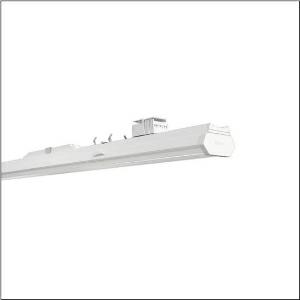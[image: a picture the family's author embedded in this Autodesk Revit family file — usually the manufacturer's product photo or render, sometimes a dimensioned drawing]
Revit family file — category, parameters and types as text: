
# Revit family: licross_21_protected_ho_52tp11mn4fxs
name_source: partatom
category: Lighting Fixtures
units: mm (PartAtom-declared; Revit-internal decimal feet)

## family parameters
Cut with Voids When Loaded = No
Host = Face
Light Source = No
Part Type = Normal
Room Calculation Point = No
Round Connector Dimension = Use Diameter
Shared = No

## types (1)
- --- (1 x LED, 15020 lm, 83.2 W, 4000K)
    Apparent Load = 83 VA
    CIE Flux Codes = 84 94 98 99 100
    Color Rendering = 80
    Color Temperature = 4000K
    Default Elevation = 1800 mm
    Description = Licross 21 Protected HO, luminaire insert, of sheet steel, galvanised, coil coated, white, length: 1.500mm, width: 66mm, height: 67mm, LED rated luminous flux: 15.020lm, light colour: 840, SDCM (Standard Deviation of Colour Matching)MacAdam ≤ 3 SDCM (initial), control gear: ON/OFF Multilumen, with plug, 3-pole, with phase selection, mains connection: 220..240V, AC, 50/60Hz, rated input power: 83W, internal wiring halogen-free, primary light control with lens, of plastic, primary optical cover: cover, of PMMA, light emission: direct distribution, primary light characteristic: symmetric, protection rating (complete): IP64, insulation class (complete): insulation class I (protective earthing), certification: CE, ENEC, VDE, UKCA, protection symbol: D if used in an environment with conductive dust loads with corresponding accessories, impact resistance: IK06, permissible ambient temperature for indoor applications: -35..+35°C, corresponds to IFS (International Featured Standards) requirements for safety and quality in the food industry, reducing of maximum allowable ambient temperature of 5°C with ceiling mounting, LABS conformity tested according to VDMA 24364:2018-05, The light source and the operating device comply with the requirements of the Ecodesign Regulation (EU) 2019/2020 and are replaceable in accordance with this regulation, packaging unit: 1 piece
    Height = 92 mm
    Lamp = 1 x LED
    Lamp Light Flux = 15020 lm
    Lamp Power = 83.2 W
    Lamp count = 1
    Length = 1500 mm
    Luminous efficacy = 181 lm/W
    Manufacturer = Siteco
    ModVariant = No
    Model = 52TP11MN4FXS
    Mounting Place = Ceiling
    Mounting Type = Pendant
    Number of Poles = 1
    OnlyDefault = Yes
    Power Factor = 1
    Product Name = Licross 21 Protected HO
    Product group = luminaire insert | ceiling pendant
    ProductGroupID = 901
    Protection Class = Protection class I
    Protection Degree = IP 64
    RLX_Detail_Level = 1
    RLX_Emergency_Light_Flux = 0 lm
    RLX_Emergency_Type = 0
    RLX_Emergency_Type_DB = No
    RlxData = <blob elided: 22181 chars, md5=89f81766>
    Socket = socket
    Standby Power = 0 W
    System Light Flux = 15020 lm
    System Power = 83 W
    Type Comments = factory setting: luminous flux: 100 % | (A | C | E) | 195 mA
    Type Image = l_1256148.jpg
    URL = http://relux.com
    VarID = @adj_109039
    Voltage = 0 V
    Weight = 0.00 kg
    Width = 88 mm

## geometry (parser evidence)
native form markers: Blend x4, Sweep x13
no freeform markers — native parametric forms only
